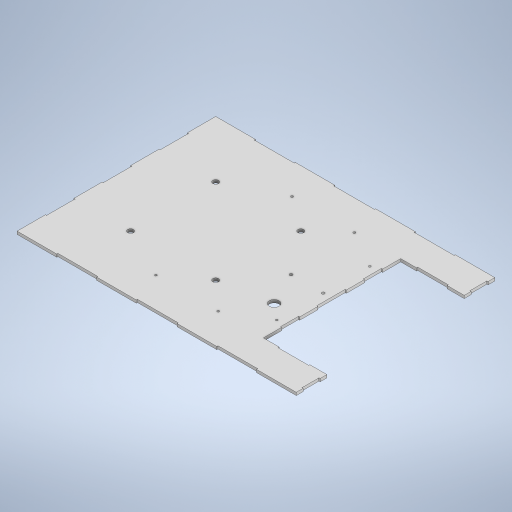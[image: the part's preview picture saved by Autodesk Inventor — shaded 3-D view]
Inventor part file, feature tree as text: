
AUTODESK INVENTOR PART (.ipt)
format: ipt  version: 2023 (Build 270158000, 158)  size: 405,504 bytes
history: native  units: mm
features: sketch x7, extrude x6, pattern_linear x1, plane x1, mirror x1
ambient origin geometry x8: Origin, YZ Plane, XZ Plane, XY Plane, X Axis, Y Axis, Z Axis, Center Point
bodies: Solid1 (feature_tree)
feature tree (16):
  extrude  "Extrusion1"  Depth=492.0mm
  extrude  "Extrusion2"  Depth=112.0mm
  extrude  "Extrusion3"  Depth=54.0mm
  pattern_linear  "Rectangular Pattern1"  Spacing1=2.0mm  [1 undecoded]
  extrude  "Extrusion4"  Depth=50.0mm
  sketch  "Sketch6"  dims[d8=2.0mm]
  plane  "Work Plane2"
  mirror  "Mirror1"
  extrude  "Extrusion5"  Depth=50.0mm
  extrude  "Extrusion6"  Depth=50.0mm
  sketch  "Sketch1"  dims[d0=350.0mm d1=492.0mm]
  sketch  "Sketch2"  dims[d2=112.0mm d3=112.0mm]
  sketch  "Sketch3"  dims[d4=54.0mm d5=54.0mm]
  sketch  "Sketch5"  dims[d6=5.0mm d7=0.0mm]
  sketch  "Sketch8"  dims[d9=2.0mm]
  sketch  "Sketch9"  dims[d10=2.0mm d11=2.0mm d12=50.0mm d13=50.0mm d14=50.0mm d15=50.0mm d16=50.0mm d17=50.0mm d18=12.0mm d19=12.0mm d20=12.0mm d21=12.0mm d22=70.0mm d23=70.0mm d24=72.0mm d25=70.0mm d26=70.0mm d27=70.0mm d28=2.0mm d29=2.0mm d30=30.0mm d32=2.0mm d33=2.0mm d34=2.0mm d35=32.0mm d36=32.0mm d37=32.0mm d39=32.0mm d40=32.0mm d41=32.0mm d42=50.0mm d43=10.0mm d44=0.0mm d45=72.0mm d46=70.0mm d47=28.0mm d48=28.0mm d49=54.0mm d50=54.0mm d51=30.0mm d52=100.0mm d53=100.0mm d54=10.0mm d55=10.0mm d56=0.0mm d57=20.0mm d59=150.0mm d60=20.0mm d62=150.0mm d63=15.53mm d64=3.8mm d65=80.53mm d66=3.8mm d67=3.8mm d68=190.53mm d69=55.0mm d70=55.0mm d71=93.0mm d72=10.0mm d73=0.0mm d78=5.0mm d79=121.0mm d80=121.0mm d81=15.75mm d82=56.5mm d83=5.0mm d84=10.0mm d85=0.0mm d86=17.0mm d87=116.0mm d88=43.0mm d89=10.0mm d90=0.0mm]
note: 1 required parameter value undecoded (feature->parameter linkage not recoverable at this tier; creation-order binding heuristic only, values carry confidence <= 0.55)
